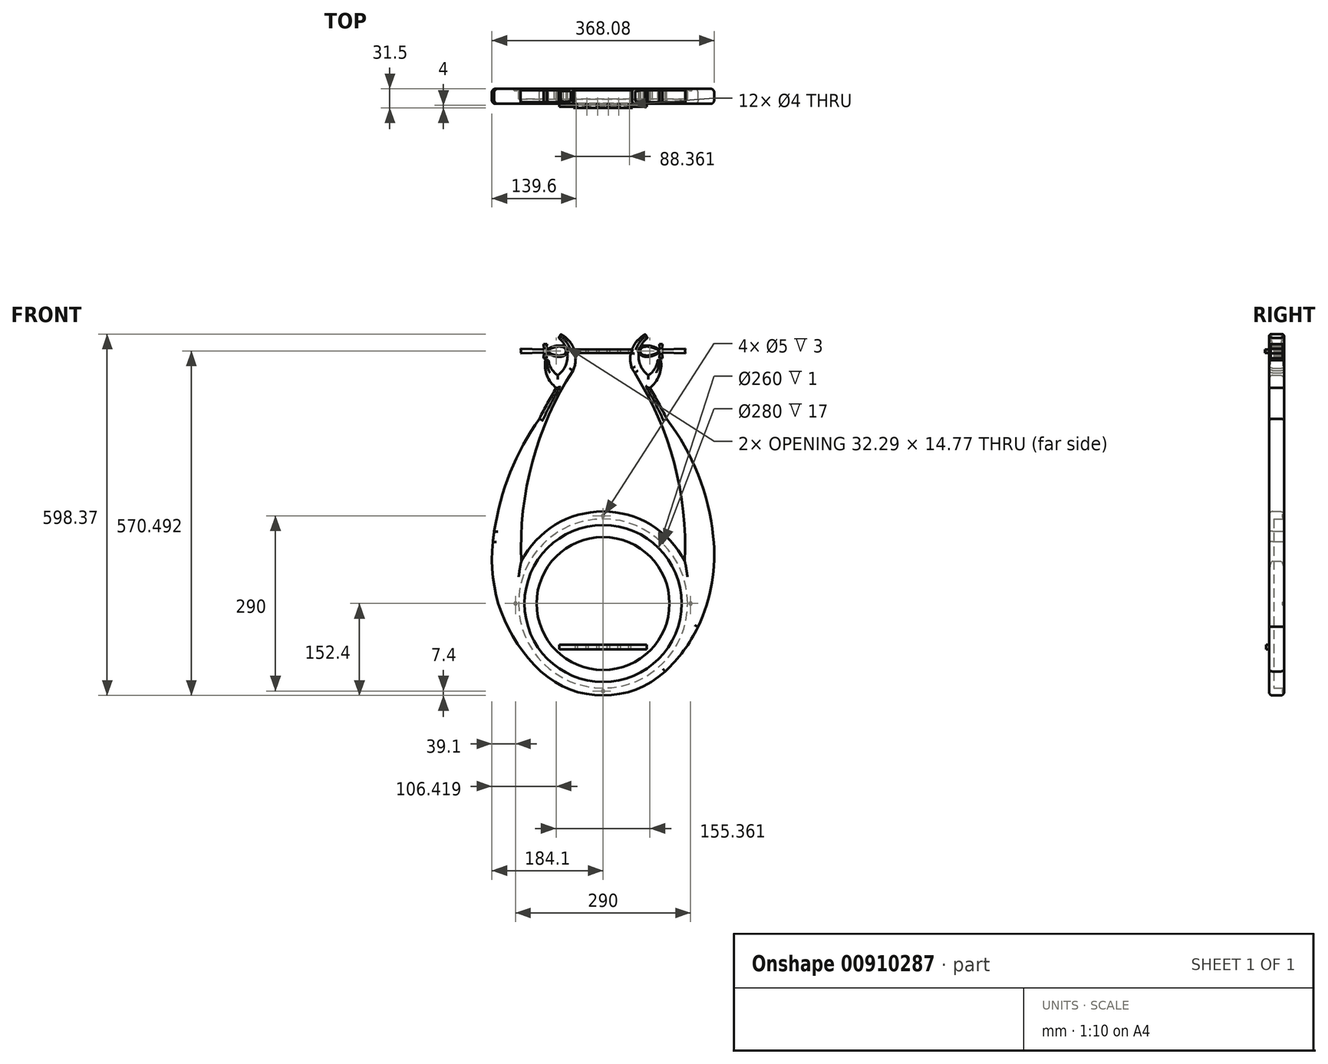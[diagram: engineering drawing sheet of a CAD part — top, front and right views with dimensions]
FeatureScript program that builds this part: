
annotation { "Feature Type Name" : "Feature", "Feature Type Description" : "" }
export const myFeature = defineFeature(function(context is Context, id is Id, definition is map)
    precondition{}
    {
        {
            var Q0;
            Q0=qCreatedBy(makeId("Front.planeOp"),FACE);
            var sketch = newSketch(context, id + "F0", { "sketchPlane" : qUnion([Q0])});
            skArc(sketch, "E0", {"start": v(-102.81, -112.5) * mm, "mid": v(0, -152.4) * mm, "end": v(102.81, -112.5) * mm});
            skArc(sketch, "E1", {"start": v(-77.27, 356.97) * mm, "mid": v(-91.95, 331.84) * mm, "end": v(-105.27, 305.96) * mm});
            skArc(sketch, "E2", {"start": v(105.27, 305.96) * mm, "mid": v(91.95, 331.84) * mm, "end": v(77.27, 356.97) * mm});
            skArc(sketch, "E3", {"start": v(-67.27, 356.97) * mm, "mid": v(-121.3, 218.22) * mm, "end": v(-135.37, 70) * mm});
            skLineSegment(sketch, "E4", {"start": v(0, 0) * mm, "end": v(0, 365.5) * mm, "construction": true});
            skArc(sketch, "E5", {"start": v(-49.84, 385.97) * mm, "mid": v(-58.78, 371.6) * mm, "end": v(-67.27, 356.97) * mm});
            skArc(sketch, "E6", {"start": v(-53.11, 430.97) * mm, "mid": v(-60.83, 439.18) * mm, "end": v(-69.82, 445.97) * mm});
            skLineSegment(sketch, "E7", {"start": v(-69.82, 445.97) * mm, "end": v(-73.43, 439.97) * mm});
            skArc(sketch, "E8", {"start": v(-75.07, 377.97) * mm, "mid": v(-58.76, 408.56) * mm, "end": v(-73.43, 439.97) * mm});
            skPoint(sketch, "E9.orphan", {"position": v(-39.82, 400.97) * mm});
            skArc(sketch, "E10", {"start": v(-90.57, 402.97) * mm, "mid": v(-85.57, 388.76) * mm, "end": v(-75.07, 377.97) * mm});
            skLineSegment(sketch, "E11", {"start": v(-90.57, 402.97) * mm, "end": v(-95.57, 402.97) * mm});
            skArc(sketch, "E12", {"start": v(-95.57, 402.97) * mm, "mid": v(-92.8, 377.42) * mm, "end": v(-77.27, 356.97) * mm});
            skArc(sketch, "E13", {"start": v(-50.7, 426.92) * mm, "mid": v(-51.87, 428.97) * mm, "end": v(-53.11, 430.97) * mm});
            skArc(sketch, "E14.MirrorCS", {"start": v(67.27, 356.97) * mm, "mid": v(121.3, 218.22) * mm, "end": v(135.37, 70) * mm});
            skArc(sketch, "E15.MirrorCS", {"start": v(95.57, 402.97) * mm, "mid": v(92.8, 377.42) * mm, "end": v(77.27, 356.97) * mm});
            skArc(sketch, "E16.MirrorCS", {"start": v(90.57, 402.97) * mm, "mid": v(85.57, 388.76) * mm, "end": v(75.07, 377.97) * mm});
            skLineSegment(sketch, "E17.MirrorCS", {"start": v(90.57, 402.97) * mm, "end": v(95.57, 402.97) * mm});
            skArc(sketch, "E18.MirrorCS", {"start": v(75.07, 377.97) * mm, "mid": v(58.76, 408.56) * mm, "end": v(73.43, 439.97) * mm});
            skLineSegment(sketch, "E19.MirrorCS", {"start": v(69.82, 445.97) * mm, "end": v(73.43, 439.97) * mm});
            skArc(sketch, "E20.MirrorCS", {"start": v(53.11, 430.97) * mm, "mid": v(60.83, 439.18) * mm, "end": v(69.82, 445.97) * mm});
            skArc(sketch, "E21.MirrorCS", {"start": v(45.98, 415.18) * mm, "mid": v(48.94, 423.35) * mm, "end": v(53.11, 430.97) * mm});
            skArc(sketch, "E22.MirrorCS", {"start": v(52.4, 381.97) * mm, "mid": v(49.96, 385.78) * mm, "end": v(47.74, 389.72) * mm});
            skArc(sketch, "E23.MirrorCS", {"start": v(49.84, 385.97) * mm, "mid": v(58.78, 371.6) * mm, "end": v(67.27, 356.97) * mm});
            skArc(sketch, "E24.trimOffspring", {"start": v(135.37, 70) * mm, "mid": v(0, 152.4) * mm, "end": v(-135.37, 70) * mm});
            skPoint(sketch, "E25.orphan", {"position": v(-44.02, 397.97) * mm});
            skArc(sketch, "E26", {"start": v(-49.84, 385.97) * mm, "mid": v(-45.46, 406.54) * mm, "end": v(-50.7, 426.92) * mm});
            skArc(sketch, "E27", {"start": v(45.98, 415.18) * mm, "mid": v(45.14, 402.33) * mm, "end": v(47.74, 389.72) * mm});
            skPoint(sketch, "E28.orphan", {"position": v(44.02, 397.97) * mm});
            skPoint(sketch, "E29.orphan", {"position": v(-153.73, 164.99) * mm});
            skPoint(sketch, "E30.orphan", {"position": v(150.74, 163.69) * mm});
            skArc(sketch, "E31", {"start": v(-182.37, 102.33) * mm, "mid": v(-168.4, -14.65) * mm, "end": v(-102.81, -112.5) * mm});
            skArc(sketch, "E32", {"start": v(102.81, -112.5) * mm, "mid": v(133.42, -78.1) * mm, "end": v(157.25, -38.7) * mm});
            skPoint(sketch, "E33.orphan", {"position": v(146.2, -43.03) * mm});
            skPoint(sketch, "E34.end.orphan", {"position": v(-146.2, -43.03) * mm});
            skArc(sketch, "E35", {"start": v(157.25, -38.7) * mm, "mid": v(180.1, 34.24) * mm, "end": v(182.37, 110.63) * mm});
            skPoint(sketch, "E35.startSnap0", {"position": v(157.25, 188.12) * mm});
            skArc(sketch, "E36", {"start": v(-180.13, 119.66) * mm, "mid": v(-181.4, 111) * mm, "end": v(-182.37, 102.33) * mm});
            skPoint(sketch, "E37.orphan", {"position": v(-162.96, 173.92) * mm});
            skPoint(sketch, "E38.orphan", {"position": v(160.9, 173.92) * mm});
            skArc(sketch, "E39", {"start": v(-105.27, 305.96) * mm, "mid": v(-156.8, 209.06) * mm, "end": v(-182.37, 102.33) * mm});
            skArc(sketch, "E40", {"start": v(182.37, 110.63) * mm, "mid": v(157.46, 213.68) * mm, "end": v(105.27, 305.96) * mm});
            skPoint(sketch, "E41.orphan", {"position": v(162.49, 188.3) * mm});
            skPoint(sketch, "E42.orphan", {"position": v(-159.18, 188.3) * mm});
            skSolve(sketch);
        }
        {
            var Q0;
            Q0 = qSketchRegion(id + "F0", true);
            extrude(context, id + "F1", {"entities" : qUnion([Q0]), "depth" : 25 * mm, "offsetDistance" : 25 * mm});
        }
        {
            var Q0;
            Q0=makeQuery(id+"F96qqXRXt9k63Jo_1.opFillet","SPLIT",FACE,{"disambiguationData":[OD(2.0)],"derivedFrom":makeQuery(id+"F1.opExtrude","CAP_FACE",FACE,{"disambiguationData":[OSD([sQuery(id+"F0.wireOp",EDGE,"E0"),sQuery(id+"F0.wireOp",EDGE,"E1"),sQuery(id+"F0.wireOp",EDGE,"E2"),sQuery(id+"F0.wireOp",EDGE,"E3"),sQuery(id+"F0.wireOp",EDGE,"E5"),sQuery(id+"F0.wireOp",EDGE,"E6"),sQuery(id+"F0.wireOp",EDGE,"E7"),sQuery(id+"F0.wireOp",EDGE,"E8"),sQuery(id+"F0.wireOp",EDGE,"E10"),sQuery(id+"F0.wireOp",EDGE,"E11"),sQuery(id+"F0.wireOp",EDGE,"E12"),sQuery(id+"F0.wireOp",EDGE,"E13"),sQuery(id+"F0.wireOp",EDGE,"E14.MirrorCS"),sQuery(id+"F0.wireOp",EDGE,"E15.MirrorCS"),sQuery(id+"F0.wireOp",EDGE,"E16.MirrorCS"),sQuery(id+"F0.wireOp",EDGE,"E17.MirrorCS"),sQuery(id+"F0.wireOp",EDGE,"E18.MirrorCS"),sQuery(id+"F0.wireOp",EDGE,"E19.MirrorCS"),sQuery(id+"F0.wireOp",EDGE,"E20.MirrorCS"),sQuery(id+"F0.wireOp",EDGE,"E21.MirrorCS"),sQuery(id+"F0.wireOp",EDGE,"E22.MirrorCS"),sQuery(id+"F0.wireOp",EDGE,"E23.MirrorCS"),sQuery(id+"F0.wireOp",EDGE,"E24.trimOffspring"),sQuery(id+"F0.wireOp",EDGE,"E26"),sQuery(id+"F0.wireOp",EDGE,"E27")])],"isStart":false})});
            var sketch = newSketch(context, id + "F2", { "sketchPlane" : qUnion([Q0])});
            skCircle(sketch, "E43", {"center": v(0, 0) * mm, "radius": 130 * mm});
            skCircle(sketch, "E44", {"center": v(0, 0) * mm, "radius": 110 * mm});
            skSolve(sketch);
        }
        {
            var Q0;
            Q0 = qSketchRegion(id + "F2", true);
            extrude(context, id + "F3", {"entities" : qUnion([Q0]), "operationType" : NewBodyOperationType.REMOVE, "oppositeDirection" : true, "depth" : 1 * mm, "offsetDistance" : 25 * mm});
        }
        {
            var Q0;
            Q0=makeQuery(id+"F96qqXRXt9k63Jo_1.opFillet","SPLIT",FACE,{"disambiguationData":[OD(2.0)],"derivedFrom":makeQuery(id+"F1.opExtrude","CAP_FACE",FACE,{"disambiguationData":[OSD([sQuery(id+"F0.wireOp",EDGE,"E0"),sQuery(id+"F0.wireOp",EDGE,"E1"),sQuery(id+"F0.wireOp",EDGE,"E2"),sQuery(id+"F0.wireOp",EDGE,"E3"),sQuery(id+"F0.wireOp",EDGE,"E5"),sQuery(id+"F0.wireOp",EDGE,"E6"),sQuery(id+"F0.wireOp",EDGE,"E7"),sQuery(id+"F0.wireOp",EDGE,"E8"),sQuery(id+"F0.wireOp",EDGE,"E10"),sQuery(id+"F0.wireOp",EDGE,"E11"),sQuery(id+"F0.wireOp",EDGE,"E12"),sQuery(id+"F0.wireOp",EDGE,"E13"),sQuery(id+"F0.wireOp",EDGE,"E14.MirrorCS"),sQuery(id+"F0.wireOp",EDGE,"E15.MirrorCS"),sQuery(id+"F0.wireOp",EDGE,"E16.MirrorCS"),sQuery(id+"F0.wireOp",EDGE,"E17.MirrorCS"),sQuery(id+"F0.wireOp",EDGE,"E18.MirrorCS"),sQuery(id+"F0.wireOp",EDGE,"E19.MirrorCS"),sQuery(id+"F0.wireOp",EDGE,"E20.MirrorCS"),sQuery(id+"F0.wireOp",EDGE,"E21.MirrorCS"),sQuery(id+"F0.wireOp",EDGE,"E22.MirrorCS"),sQuery(id+"F0.wireOp",EDGE,"E23.MirrorCS"),sQuery(id+"F0.wireOp",EDGE,"E24.trimOffspring"),sQuery(id+"F0.wireOp",EDGE,"E26"),sQuery(id+"F0.wireOp",EDGE,"E27")])],"isStart":true})});
            cPlane(context, id + "F4", {"entities" : qUnion([Q0]), "cplaneType" : CPlaneType.OFFSET, "offset" : 12.5 * mm, "oppositeDirection" : true, "width" : 150 * mm, "height" : 150 * mm});
        }
        {
            var Q0;
            Q0=qCreatedBy(id+"F4.planeOp",FACE);
            var sketch = newSketch(context, id + "F5", { "sketchPlane" : qUnion([Q0])});
            skLineSegment(sketch, "E45.bottom", {"start": v(-60.13, 415.18) * mm, "end": v(60.13, 415.18) * mm});
            skLineSegment(sketch, "E45.top", {"start": v(-60.13, 420.82) * mm, "end": v(60.13, 420.82) * mm});
            skPoint(sketch, "E45.middle", {"position": v(0, 418) * mm});
            skArc(sketch, "E46", {"start": v(62.57, 425.82) * mm, "mid": v(61.07, 423.46) * mm, "end": v(60.13, 420.82) * mm});
            skArc(sketch, "E47", {"start": v(93.83, 420.5) * mm, "mid": v(87.75, 423.53) * mm, "end": v(81.35, 425.82) * mm});
            skArc(sketch, "E48", {"start": v(81.35, 409.82) * mm, "mid": v(87.76, 412.29) * mm, "end": v(93.83, 415.5) * mm});
            skLineSegment(sketch, "E49", {"start": v(93.83, 420.5) * mm, "end": v(93, 429.81) * mm});
            skLineSegment(sketch, "E50", {"start": v(98.28, 429.84) * mm, "end": v(97.83, 420.5) * mm});
            skLineSegment(sketch, "E51", {"start": v(93.83, 415.5) * mm, "end": v(93.27, 406.17) * mm});
            skLineSegment(sketch, "E52", {"start": v(98.28, 406.16) * mm, "end": v(97.83, 415.5) * mm});
            skLineSegment(sketch, "E53", {"start": v(97.83, 415.5) * mm, "end": v(136.4, 414) * mm});
            skLineSegment(sketch, "E54", {"start": v(136.4, 422) * mm, "end": v(97.83, 420.5) * mm});
            skArc(sketch, "E55", {"start": v(136.4, 422) * mm, "mid": v(135.93, 418) * mm, "end": v(136.4, 414) * mm});
            skArc(sketch, "E56", {"start": v(93, 429.81) * mm, "mid": v(95.64, 429.62) * mm, "end": v(98.28, 429.84) * mm});
            skArc(sketch, "E57", {"start": v(98.28, 406.16) * mm, "mid": v(95.77, 406.35) * mm, "end": v(93.27, 406.17) * mm});
            skArc(sketch, "E58.trimOffspring", {"start": v(60.13, 415.18) * mm, "mid": v(61.07, 412.54) * mm, "end": v(62.57, 410.18) * mm});
            skLineSegment(sketch, "E59", {"start": v(0, 418) * mm, "end": v(0, 365.49) * mm, "construction": true});
            skArc(sketch, "E60.MirrorCS", {"start": v(-98.28, 406.16) * mm, "mid": v(-95.77, 406.35) * mm, "end": v(-93.27, 406.17) * mm});
            skArc(sketch, "E61.MirrorCS", {"start": v(-136.4, 422) * mm, "mid": v(-135.93, 418) * mm, "end": v(-136.4, 414) * mm});
            skArc(sketch, "E62.MirrorCS", {"start": v(-93, 429.81) * mm, "mid": v(-95.64, 429.62) * mm, "end": v(-98.28, 429.84) * mm});
            skLineSegment(sketch, "E63.MirrorCS", {"start": v(-98.28, 429.84) * mm, "end": v(-97.83, 420.5) * mm});
            skLineSegment(sketch, "E64.MirrorCS", {"start": v(-93.83, 415.5) * mm, "end": v(-93.27, 406.17) * mm});
            skArc(sketch, "E65.MirrorCS", {"start": v(-81.35, 409.82) * mm, "mid": v(-87.76, 412.29) * mm, "end": v(-93.83, 415.5) * mm});
            skLineSegment(sketch, "E66.MirrorCS", {"start": v(-93.83, 420.5) * mm, "end": v(-93, 429.81) * mm});
            skLineSegment(sketch, "E67.MirrorCS", {"start": v(-136.4, 422) * mm, "end": v(-97.83, 420.5) * mm});
            skLineSegment(sketch, "E68.MirrorCS", {"start": v(-97.83, 415.5) * mm, "end": v(-136.4, 414) * mm});
            skArc(sketch, "E69.MirrorCS", {"start": v(-93.83, 420.5) * mm, "mid": v(-87.75, 423.53) * mm, "end": v(-81.35, 425.82) * mm});
            skLineSegment(sketch, "E70.MirrorCS", {"start": v(-98.28, 406.16) * mm, "end": v(-97.83, 415.5) * mm});
            skArc(sketch, "E71.MirrorCS", {"start": v(-62.57, 425.82) * mm, "mid": v(-61.07, 423.46) * mm, "end": v(-60.13, 420.82) * mm});
            skArc(sketch, "E72.MirrorCS", {"start": v(-60.13, 415.18) * mm, "mid": v(-61.07, 412.54) * mm, "end": v(-62.57, 410.18) * mm});
            skArc(sketch, "E73", {"start": v(81.35, 425.82) * mm, "mid": v(71.96, 427.2) * mm, "end": v(62.57, 425.82) * mm});
            skPoint(sketch, "E73.startSnap0", {"position": v(62.57, 425.82) * mm});
            skArc(sketch, "E74", {"start": v(62.57, 410.18) * mm, "mid": v(71.93, 408.61) * mm, "end": v(81.35, 409.82) * mm});
            skPoint(sketch, "E74.startSnap0", {"position": v(82.44, 410.18) * mm});
            skPoint(sketch, "E75.orphan", {"position": v(64.98, 428.1) * mm});
            skPoint(sketch, "E76.orphan", {"position": v(66.07, 407.2) * mm});
            skArc(sketch, "E77.MirrorCS", {"start": v(-81.35, 425.82) * mm, "mid": v(-71.96, 427.2) * mm, "end": v(-62.57, 425.82) * mm});
            skArc(sketch, "E78.MirrorCS", {"start": v(-62.57, 410.18) * mm, "mid": v(-71.93, 408.61) * mm, "end": v(-81.35, 409.82) * mm});
            skPoint(sketch, "E79.orphan", {"position": v(-66.07, 407.2) * mm});
            skPoint(sketch, "E80.orphan", {"position": v(-64.98, 428.1) * mm});
            skPoint(sketch, "E81.orphan", {"position": v(85.85, 411.46) * mm});
            skPoint(sketch, "E82.orphan", {"position": v(-81.35, 425.82) * mm});
            skPoint(sketch, "E83.orphan", {"position": v(-85.85, 411.46) * mm});
            skSolve(sketch);
        }
        {
            var Q0;
            Q0 = qSketchRegion(id + "F5", true);
            extrude(context, id + "F6", {"entities" : qUnion([Q0]), "operationType" : NewBodyOperationType.ADD, "depth" : 10 * mm, "offsetDistance" : 25 * mm, "hasSecondDirection" : true, "secondDirectionOppositeDirection" : true, "secondDirectionDepth" : 10 * mm});
        }
        {
            var Q0;
            Q0=makeQuery(id+"F6.opExtrude","SWEPT_EDGE",EDGE,{"disambiguationData":[OSD([sQuery(id+"F5.wireOp",EDGE,"E58.trimOffspring"),sQuery(id+"F5.wireOp",EDGE,"E74")])]});
            var Q1;
            Q1=makeQuery(id+"F6.opExtrude","SWEPT_EDGE",EDGE,{"disambiguationData":[OSD([sQuery(id+"F5.wireOp",EDGE,"E46"),sQuery(id+"F5.wireOp",EDGE,"E73")])]});
            var Q2;
            Q2=makeQuery(id+"F6.opExtrude","SWEPT_EDGE",EDGE,{"disambiguationData":[OSD([sQuery(id+"F5.wireOp",EDGE,"E72.MirrorCS"),sQuery(id+"F5.wireOp",EDGE,"E78.MirrorCS")])]});
            var Q3;
            Q3=makeQuery(id+"F6.opExtrude","SWEPT_EDGE",EDGE,{"disambiguationData":[OSD([sQuery(id+"F5.wireOp",EDGE,"E71.MirrorCS"),sQuery(id+"F5.wireOp",EDGE,"E77.MirrorCS")])]});
            fillet(context, id + "F7", {"entities" : qUnion([Q0, Q1, Q2, Q3]), "radius" : 10 * mm, "tangentPropagation" : true, "allowEdgeOverflow" : false});
        }
        {
            var Q0;
            {var subQ0=sQuery(id+"F5.wireOp",EDGE,"E52");var subQ1=sQuery(id+"F5.wireOp",EDGE,"E51");var subQ2=sQuery(id+"F5.wireOp",EDGE,"E50");var subQ3=sQuery(id+"F5.wireOp",EDGE,"E74");var subQ4=sQuery(id+"F5.wireOp",EDGE,"E49");var subQ5=sQuery(id+"F5.wireOp",EDGE,"E73");var subQ6=sQuery(id+"F5.wireOp",EDGE,"E48");var subQ7=sQuery(id+"F5.wireOp",EDGE,"E47");var subQ9=sQuery(id+"F5.wireOp",EDGE,"E58.trimOffspring");var subQ10=sQuery(id+"F5.wireOp",EDGE,"E45.bottom");var subQ11=sQuery(id+"F5.wireOp",EDGE,"E45.top");var subQ12=sQuery(id+"F5.wireOp",EDGE,"E46");var subQ13=sQuery(id+"F5.wireOp",EDGE,"E53");var subQ14=sQuery(id+"F5.wireOp",EDGE,"E54");var subQ15=sQuery(id+"F5.wireOp",EDGE,"E55");var subQ16=sQuery(id+"F5.wireOp",EDGE,"E56");var subQ17=sQuery(id+"F5.wireOp",EDGE,"E57");Q0=makeQuery(id+"F6.boolean.opBoolean","SPLIT",FACE,{"disambiguationData":[TD([makeQuery(id+"F6.opExtrude","SWEPT_FACE",FACE,{"disambiguationData":[OSD([subQ12])]})])],"derivedFrom":makeQuery(id+"F6.opExtrude","CAP_FACE",FACE,{"disambiguationData":[OSD([subQ10,subQ11,subQ12,subQ7,subQ6,subQ4,subQ2,subQ1,subQ0,subQ13,subQ14,subQ15,subQ16,subQ17,subQ9,sQuery(id+"F5.wireOp",EDGE,"E60.MirrorCS"),sQuery(id+"F5.wireOp",EDGE,"E61.MirrorCS"),sQuery(id+"F5.wireOp",EDGE,"E62.MirrorCS"),sQuery(id+"F5.wireOp",EDGE,"E63.MirrorCS"),sQuery(id+"F5.wireOp",EDGE,"E64.MirrorCS"),sQuery(id+"F5.wireOp",EDGE,"E65.MirrorCS"),sQuery(id+"F5.wireOp",EDGE,"E66.MirrorCS"),sQuery(id+"F5.wireOp",EDGE,"E67.MirrorCS"),sQuery(id+"F5.wireOp",EDGE,"E68.MirrorCS"),sQuery(id+"F5.wireOp",EDGE,"E69.MirrorCS"),sQuery(id+"F5.wireOp",EDGE,"E70.MirrorCS"),sQuery(id+"F5.wireOp",EDGE,"E71.MirrorCS"),sQuery(id+"F5.wireOp",EDGE,"E72.MirrorCS"),subQ5,subQ3,sQuery(id+"F5.wireOp",EDGE,"E77.MirrorCS"),sQuery(id+"F5.wireOp",EDGE,"E78.MirrorCS")])],"isStart":true})});}
            var sketch = newSketch(context, id + "F8", { "sketchPlane" : qUnion([Q0])});
            skPoint(sketch, "E84", {"position": v(-93.83, 418.38) * mm});
            skPoint(sketch, "E84.positionSnap0", {"position": v(-58.06, 418.38) * mm});
            skArc(sketch, "E85", {"start": v(-77.83, 424.7) * mm, "mid": v(-86.09, 422.2) * mm, "end": v(-93.83, 418.38) * mm});
            skArc(sketch, "E86", {"start": v(-93.83, 418.38) * mm, "mid": v(-86.32, 413.66) * mm, "end": v(-77.83, 411.08) * mm});
            skArc(sketch, "E87", {"start": v(-66.05, 424.4) * mm, "mid": v(-71.92, 425.48) * mm, "end": v(-77.83, 424.7) * mm});
            skArc(sketch, "E88", {"start": v(-77.83, 411.08) * mm, "mid": v(-71.9, 410.74) * mm, "end": v(-66.05, 411.69) * mm});
            skArc(sketch, "E89", {"start": v(-66.05, 411.69) * mm, "mid": v(-61.54, 418.05) * mm, "end": v(-66.05, 424.4) * mm});
            skLineSegment(sketch, "E90", {"start": v(0, 410.89) * mm, "end": v(0, 363.53) * mm, "construction": true});
            skArc(sketch, "E91.MirrorCS", {"start": v(66.05, 411.69) * mm, "mid": v(61.54, 418.05) * mm, "end": v(66.05, 424.4) * mm});
            skArc(sketch, "E92.MirrorCS", {"start": v(93.83, 418.38) * mm, "mid": v(86.32, 413.66) * mm, "end": v(77.83, 411.08) * mm});
            skArc(sketch, "E93.MirrorCS", {"start": v(77.83, 424.7) * mm, "mid": v(86.09, 422.2) * mm, "end": v(93.83, 418.38) * mm});
            skArc(sketch, "E94.MirrorCS", {"start": v(66.05, 424.4) * mm, "mid": v(71.92, 425.48) * mm, "end": v(77.83, 424.7) * mm});
            skArc(sketch, "E95.MirrorCS", {"start": v(77.83, 411.08) * mm, "mid": v(71.9, 410.74) * mm, "end": v(66.05, 411.69) * mm});
            skPoint(sketch, "E96.MirrorP", {"position": v(58.06, 418.38) * mm});
            skPoint(sketch, "E97.MirrorP", {"position": v(93.83, 418.38) * mm});
            skSolve(sketch);
        }
        {
            var Q0;
            Q0 = qSketchRegion(id + "F8", true);
            extrude(context, id + "F9", {"entities" : qUnion([Q0]), "operationType" : NewBodyOperationType.REMOVE, "endBound" : BoundingType.THROUGH_ALL, "oppositeDirection" : true, "depth" : 25 * mm, "offsetDistance" : 25 * mm});
        }
        {
            var Q0;
            Q0=makeQuery(id+"F1.opExtrude","CAP_EDGE",EDGE,{"disambiguationData":[OSD([sQuery(id+"F0.wireOp",EDGE,"E18.MirrorCS")])],"isStart":false});
            var Q1;
            Q1=makeQuery(id+"F1.opExtrude","CAP_EDGE",EDGE,{"disambiguationData":[OSD([sQuery(id+"F0.wireOp",EDGE,"E32")])],"isStart":false});
            var Q2;
            Q2=makeQuery(id+"F1.opExtrude","CAP_EDGE",EDGE,{"disambiguationData":[OSD([sQuery(id+"F0.wireOp",EDGE,"E2")])],"isStart":false});
            var Q3;
            Q3=makeQuery(id+"F1.opExtrude","CAP_EDGE",EDGE,{"disambiguationData":[OSD([sQuery(id+"F0.wireOp",EDGE,"E40")])],"isStart":false});
            var Q4;
            Q4=makeQuery(id+"F1.opExtrude","CAP_EDGE",EDGE,{"disambiguationData":[OSD([sQuery(id+"F0.wireOp",EDGE,"E35")])],"isStart":false});
            var Q5;
            Q5=makeQuery(id+"F1.opExtrude","CAP_EDGE",EDGE,{"disambiguationData":[OSD([sQuery(id+"F0.wireOp",EDGE,"E15.MirrorCS")])],"isStart":false});
            var Q6;
            Q6=makeQuery(id+"F1.opExtrude","CAP_EDGE",EDGE,{"disambiguationData":[OSD([sQuery(id+"F0.wireOp",EDGE,"E0")])],"isStart":false});
            var Q7;
            Q7=makeQuery(id+"F1.opExtrude","CAP_EDGE",EDGE,{"disambiguationData":[OSD([sQuery(id+"F0.wireOp",EDGE,"E27")])],"isStart":false});
            var Q8;
            Q8=makeQuery(id+"F1.opExtrude","CAP_EDGE",EDGE,{"disambiguationData":[OSD([sQuery(id+"F0.wireOp",EDGE,"E14.MirrorCS"),sQuery(id+"F0.wireOp",EDGE,"E23.MirrorCS")])],"isStart":false});
            var Q9;
            Q9=makeQuery(id+"F1.opExtrude","CAP_EDGE",EDGE,{"disambiguationData":[OSD([sQuery(id+"F0.wireOp",EDGE,"E16.MirrorCS")])],"isStart":false});
            var Q10;
            Q10=makeQuery(id+"F1.opExtrude","CAP_EDGE",EDGE,{"disambiguationData":[OSD([sQuery(id+"F0.wireOp",EDGE,"E20.MirrorCS")])],"isStart":false});
            var Q11;
            Q11=makeQuery(id+"F1.opExtrude","CAP_EDGE",EDGE,{"disambiguationData":[OSD([sQuery(id+"F0.wireOp",EDGE,"E19.MirrorCS")])],"isStart":false});
            var Q12;
            Q12=makeQuery(id+"F1.opExtrude","CAP_EDGE",EDGE,{"disambiguationData":[OSD([sQuery(id+"F0.wireOp",EDGE,"E21.MirrorCS")])],"isStart":false});
            var Q13;
            Q13=makeQuery(id+"F1.opExtrude","CAP_EDGE",EDGE,{"disambiguationData":[OSD([sQuery(id+"F0.wireOp",EDGE,"E17.MirrorCS")])],"isStart":false});
            var Q14;
            Q14=makeQuery(id+"F1.opExtrude","CAP_EDGE",EDGE,{"disambiguationData":[OSD([sQuery(id+"F0.wireOp",EDGE,"E24.trimOffspring")])],"isStart":false});
            var Q15;
            Q15=makeQuery(id+"F1.opExtrude","CAP_EDGE",EDGE,{"disambiguationData":[OSD([sQuery(id+"F0.wireOp",EDGE,"E26")])],"isStart":false});
            var Q16;
            Q16=makeQuery(id+"F1.opExtrude","CAP_EDGE",EDGE,{"disambiguationData":[OSD([sQuery(id+"F0.wireOp",EDGE,"E6")])],"isStart":false});
            var Q17;
            Q17=makeQuery(id+"F1.opExtrude","CAP_EDGE",EDGE,{"disambiguationData":[OSD([sQuery(id+"F0.wireOp",EDGE,"E3"),sQuery(id+"F0.wireOp",EDGE,"E5")])],"isStart":false});
            var Q18;
            Q18=makeQuery(id+"F1.opExtrude","CAP_EDGE",EDGE,{"disambiguationData":[OSD([sQuery(id+"F0.wireOp",EDGE,"E13")])],"isStart":false});
            var Q19;
            Q19=makeQuery(id+"F1.opExtrude","CAP_EDGE",EDGE,{"disambiguationData":[OSD([sQuery(id+"F0.wireOp",EDGE,"E22.MirrorCS")])],"isStart":false});
            var Q20;
            Q20=makeQuery(id+"F1.opExtrude","CAP_EDGE",EDGE,{"disambiguationData":[OSD([sQuery(id+"F0.wireOp",EDGE,"E39")])],"isStart":false});
            var Q21;
            Q21=makeQuery(id+"F1.opExtrude","CAP_EDGE",EDGE,{"disambiguationData":[OSD([sQuery(id+"F0.wireOp",EDGE,"E36")])],"isStart":false});
            var Q22;
            Q22=makeQuery(id+"F1.opExtrude","CAP_EDGE",EDGE,{"disambiguationData":[OSD([sQuery(id+"F0.wireOp",EDGE,"E12")])],"isStart":false});
            var Q23;
            Q23=makeQuery(id+"F1.opExtrude","CAP_EDGE",EDGE,{"disambiguationData":[OSD([sQuery(id+"F0.wireOp",EDGE,"E10")])],"isStart":false});
            var Q24;
            Q24=makeQuery(id+"F1.opExtrude","CAP_EDGE",EDGE,{"disambiguationData":[OSD([sQuery(id+"F0.wireOp",EDGE,"E31")])],"isStart":false});
            var Q25;
            Q25=makeQuery(id+"F1.opExtrude","CAP_EDGE",EDGE,{"disambiguationData":[OSD([sQuery(id+"F0.wireOp",EDGE,"E7")])],"isStart":false});
            var Q26;
            Q26=makeQuery(id+"F1.opExtrude","CAP_EDGE",EDGE,{"disambiguationData":[OSD([sQuery(id+"F0.wireOp",EDGE,"E1")])],"isStart":false});
            var Q27;
            Q27=makeQuery(id+"F1.opExtrude","CAP_EDGE",EDGE,{"disambiguationData":[OSD([sQuery(id+"F0.wireOp",EDGE,"E8")])],"isStart":false});
            var Q28;
            Q28=makeQuery(id+"F1.opExtrude","CAP_EDGE",EDGE,{"disambiguationData":[OSD([sQuery(id+"F0.wireOp",EDGE,"E11")])],"isStart":false});
            fillet(context, id + "F10", {"entities" : qUnion([Q0, Q1, Q2, Q3, Q4, Q5, Q6, Q7, Q8, Q9, Q10, Q11, Q12, Q13, Q14, Q15, Q16, Q17, Q18, Q19, Q20, Q21, Q22, Q23, Q24, Q25, Q26, Q27, Q28]), "radius" : 6 * mm, "tangentPropagation" : true, "allowEdgeOverflow" : false});
        }
        {
            var Q0;
            {var subQ0=sQuery(id+"F0.wireOp",EDGE,"E24.trimOffspring");var subQ1=sQuery(id+"F0.wireOp",EDGE,"E22.MirrorCS");var subQ2=sQuery(id+"F0.wireOp",EDGE,"E21.MirrorCS");var subQ3=sQuery(id+"F0.wireOp",EDGE,"E20.MirrorCS");var subQ4=sQuery(id+"F0.wireOp",EDGE,"E19.MirrorCS");var subQ5=sQuery(id+"F0.wireOp",EDGE,"E18.MirrorCS");var subQ6=sQuery(id+"F0.wireOp",EDGE,"E17.MirrorCS");var subQ7=sQuery(id+"F0.wireOp",EDGE,"E16.MirrorCS");var subQ8=sQuery(id+"F0.wireOp",EDGE,"E15.MirrorCS");var subQ9=sQuery(id+"F0.wireOp",EDGE,"E23.MirrorCS");var subQ10=sQuery(id+"F0.wireOp",EDGE,"E14.MirrorCS");var subQ11=sQuery(id+"F0.wireOp",EDGE,"E13");var subQ12=sQuery(id+"F0.wireOp",EDGE,"E2");var subQ13=sQuery(id+"F0.wireOp",EDGE,"E1");var subQ14=sQuery(id+"F0.wireOp",EDGE,"E5");var subQ15=sQuery(id+"F0.wireOp",EDGE,"E3");var subQ16=sQuery(id+"F0.wireOp",EDGE,"E26");var subQ17=sQuery(id+"F0.wireOp",EDGE,"E0");var subQ18=sQuery(id+"F0.wireOp",EDGE,"E12");var subQ19=sQuery(id+"F0.wireOp",EDGE,"E6");var subQ20=sQuery(id+"F0.wireOp",EDGE,"E7");var subQ21=sQuery(id+"F0.wireOp",EDGE,"E8");var subQ22=sQuery(id+"F0.wireOp",EDGE,"E10");var subQ23=sQuery(id+"F0.wireOp",EDGE,"E11");var subQ24=sQuery(id+"F0.wireOp",EDGE,"E27");var subQ25=sQuery(id+"F0.wireOp",EDGE,"E31");var subQ26=sQuery(id+"F0.wireOp",EDGE,"E32");var subQ27=sQuery(id+"F0.wireOp",EDGE,"E35");var subQ28=sQuery(id+"F0.wireOp",EDGE,"E36");var subQ29=sQuery(id+"F0.wireOp",EDGE,"E39");var subQ30=sQuery(id+"F0.wireOp",EDGE,"E40");Q0=makeQuery(id+"FXKQqumeNgOc6mp_1.1.F3.boolean.opBoolean","SPLIT",FACE,{"disambiguationData":[TD([makeQuery(id+"F1.opExtrude","SWEPT_FACE",FACE,{"disambiguationData":[OSD([subQ17])]})])],"derivedFrom":makeQuery(id+"F1.opExtrude","CAP_FACE",FACE,{"disambiguationData":[OSD([subQ17,subQ13,subQ12,subQ15,subQ14,subQ19,subQ20,subQ21,subQ22,subQ23,subQ18,subQ11,subQ10,subQ8,subQ7,subQ6,subQ5,subQ4,subQ3,subQ2,subQ1,subQ9,subQ0,subQ16,subQ24,subQ25,subQ26,subQ27,subQ28,subQ29,subQ30])],"isStart":true})});}
            fillet(context, id + "F11", {"entities" : qUnion([Q0]), "radius" : 6 * mm, "tangentPropagation" : true, "allowEdgeOverflow" : false});
        }
        {
            var Q0;
            Q0=makeQuery(id+"F3.boolean.opBoolean","SPLIT",FACE,{"disambiguationData":[TD([makeQuery(id+"F3.opExtrude","SWEPT_FACE",FACE,{"disambiguationData":[OSD([sQuery(id+"F2.wireOp",EDGE,"E44")])]})])],"derivedFrom":makeQuery(id+"F1.opExtrude","CAP_FACE",FACE,{"disambiguationData":[OSD([sQuery(id+"F0.wireOp",EDGE,"E0"),sQuery(id+"F0.wireOp",EDGE,"E1"),sQuery(id+"F0.wireOp",EDGE,"E2"),sQuery(id+"F0.wireOp",EDGE,"E3"),sQuery(id+"F0.wireOp",EDGE,"E5"),sQuery(id+"F0.wireOp",EDGE,"E6"),sQuery(id+"F0.wireOp",EDGE,"E7"),sQuery(id+"F0.wireOp",EDGE,"E8"),sQuery(id+"F0.wireOp",EDGE,"E10"),sQuery(id+"F0.wireOp",EDGE,"E11"),sQuery(id+"F0.wireOp",EDGE,"E12"),sQuery(id+"F0.wireOp",EDGE,"E13"),sQuery(id+"F0.wireOp",EDGE,"E14.MirrorCS"),sQuery(id+"F0.wireOp",EDGE,"E15.MirrorCS"),sQuery(id+"F0.wireOp",EDGE,"E16.MirrorCS"),sQuery(id+"F0.wireOp",EDGE,"E17.MirrorCS"),sQuery(id+"F0.wireOp",EDGE,"E18.MirrorCS"),sQuery(id+"F0.wireOp",EDGE,"E19.MirrorCS"),sQuery(id+"F0.wireOp",EDGE,"E20.MirrorCS"),sQuery(id+"F0.wireOp",EDGE,"E21.MirrorCS"),sQuery(id+"F0.wireOp",EDGE,"E22.MirrorCS"),sQuery(id+"F0.wireOp",EDGE,"E23.MirrorCS"),sQuery(id+"F0.wireOp",EDGE,"E24.trimOffspring"),sQuery(id+"F0.wireOp",EDGE,"E26"),sQuery(id+"F0.wireOp",EDGE,"E27"),sQuery(id+"F0.wireOp",EDGE,"E31"),sQuery(id+"F0.wireOp",EDGE,"E32"),sQuery(id+"F0.wireOp",EDGE,"E35"),sQuery(id+"F0.wireOp",EDGE,"E36"),sQuery(id+"F0.wireOp",EDGE,"E39"),sQuery(id+"F0.wireOp",EDGE,"E40")])],"isStart":false})});
            var sketch = newSketch(context, id + "F12", { "sketchPlane" : qUnion([Q0])});
            skLineSegment(sketch, "E98.bottom", {"start": v(72.5, -76.2) * mm, "end": v(-72.5, -76.2) * mm});
            skLineSegment(sketch, "E98.top", {"start": v(72.5, -68.2) * mm, "end": v(-72.5, -68.2) * mm});
            skLineSegment(sketch, "E98.left", {"start": v(72.5, -76.2) * mm, "end": v(72.5, -68.2) * mm});
            skLineSegment(sketch, "E98.right", {"start": v(-72.5, -76.2) * mm, "end": v(-72.5, -68.2) * mm});
            skPoint(sketch, "E98.middle", {"position": v(0, -72.2) * mm});
            skSolve(sketch);
        }
        {
            var Q0;
            Q0 = qSketchRegion(id + "F12", true);
            extrude(context, id + "F13", {"entities" : qUnion([Q0]), "operationType" : NewBodyOperationType.ADD, "depth" : 5 * mm, "offsetDistance" : 25 * mm});
        }
        {
            var Q0;
            {var subQ0=sQuery(id+"F5.wireOp",EDGE,"E45.bottom");var subQ1=sQuery(id+"F5.wireOp",EDGE,"E45.top");Q0=makeQuery(id+"F6.boolean.opBoolean","SPLIT",FACE,{"disambiguationData":[TD([makeQuery(id+"F1.opExtrude","SWEPT_FACE",FACE,{"disambiguationData":[OSD([sQuery(id+"F0.wireOp",EDGE,"E21.MirrorCS")])]})])],"derivedFrom":makeQuery(id+"F6.opExtrude","CAP_FACE",FACE,{"disambiguationData":[OSD([subQ0,subQ1,sQuery(id+"F5.wireOp",EDGE,"E46"),sQuery(id+"F5.wireOp",EDGE,"E47"),sQuery(id+"F5.wireOp",EDGE,"E48"),sQuery(id+"F5.wireOp",EDGE,"E49"),sQuery(id+"F5.wireOp",EDGE,"E50"),sQuery(id+"F5.wireOp",EDGE,"E51"),sQuery(id+"F5.wireOp",EDGE,"E52"),sQuery(id+"F5.wireOp",EDGE,"E53"),sQuery(id+"F5.wireOp",EDGE,"E54"),sQuery(id+"F5.wireOp",EDGE,"E55"),sQuery(id+"F5.wireOp",EDGE,"E56"),sQuery(id+"F5.wireOp",EDGE,"E57"),sQuery(id+"F5.wireOp",EDGE,"E58.trimOffspring"),sQuery(id+"F5.wireOp",EDGE,"E60.MirrorCS"),sQuery(id+"F5.wireOp",EDGE,"E61.MirrorCS"),sQuery(id+"F5.wireOp",EDGE,"E62.MirrorCS"),sQuery(id+"F5.wireOp",EDGE,"E63.MirrorCS"),sQuery(id+"F5.wireOp",EDGE,"E64.MirrorCS"),sQuery(id+"F5.wireOp",EDGE,"E65.MirrorCS"),sQuery(id+"F5.wireOp",EDGE,"E66.MirrorCS"),sQuery(id+"F5.wireOp",EDGE,"E67.MirrorCS"),sQuery(id+"F5.wireOp",EDGE,"E68.MirrorCS"),sQuery(id+"F5.wireOp",EDGE,"E69.MirrorCS"),sQuery(id+"F5.wireOp",EDGE,"E70.MirrorCS"),sQuery(id+"F5.wireOp",EDGE,"E71.MirrorCS"),sQuery(id+"F5.wireOp",EDGE,"E72.MirrorCS"),sQuery(id+"F5.wireOp",EDGE,"E73"),sQuery(id+"F5.wireOp",EDGE,"E74"),sQuery(id+"F5.wireOp",EDGE,"E77.MirrorCS"),sQuery(id+"F5.wireOp",EDGE,"E78.MirrorCS")])],"isStart":true})});}
            extrude(context, id + "F14", {"entities" : qUnion([Q0]), "operationType" : NewBodyOperationType.ADD, "depth" : 9 * mm, "offsetDistance" : 25 * mm});
        }
        {
            var Q0;
            Q0=makeQuery(id+"F11.opFillet","SPLIT",FACE,{"disambiguationData":[OD(2.0)],"derivedFrom":makeQuery(id+"F1.opExtrude","CAP_FACE",FACE,{"disambiguationData":[OSD([sQuery(id+"F0.wireOp",EDGE,"E0"),sQuery(id+"F0.wireOp",EDGE,"E1"),sQuery(id+"F0.wireOp",EDGE,"E2"),sQuery(id+"F0.wireOp",EDGE,"E3"),sQuery(id+"F0.wireOp",EDGE,"E5"),sQuery(id+"F0.wireOp",EDGE,"E6"),sQuery(id+"F0.wireOp",EDGE,"E7"),sQuery(id+"F0.wireOp",EDGE,"E8"),sQuery(id+"F0.wireOp",EDGE,"E10"),sQuery(id+"F0.wireOp",EDGE,"E11"),sQuery(id+"F0.wireOp",EDGE,"E12"),sQuery(id+"F0.wireOp",EDGE,"E13"),sQuery(id+"F0.wireOp",EDGE,"E14.MirrorCS"),sQuery(id+"F0.wireOp",EDGE,"E15.MirrorCS"),sQuery(id+"F0.wireOp",EDGE,"E16.MirrorCS"),sQuery(id+"F0.wireOp",EDGE,"E17.MirrorCS"),sQuery(id+"F0.wireOp",EDGE,"E18.MirrorCS"),sQuery(id+"F0.wireOp",EDGE,"E19.MirrorCS"),sQuery(id+"F0.wireOp",EDGE,"E20.MirrorCS"),sQuery(id+"F0.wireOp",EDGE,"E21.MirrorCS"),sQuery(id+"F0.wireOp",EDGE,"E22.MirrorCS"),sQuery(id+"F0.wireOp",EDGE,"E23.MirrorCS"),sQuery(id+"F0.wireOp",EDGE,"E24.trimOffspring"),sQuery(id+"F0.wireOp",EDGE,"E26"),sQuery(id+"F0.wireOp",EDGE,"E27"),sQuery(id+"F0.wireOp",EDGE,"E31"),sQuery(id+"F0.wireOp",EDGE,"E32"),sQuery(id+"F0.wireOp",EDGE,"E35"),sQuery(id+"F0.wireOp",EDGE,"E36"),sQuery(id+"F0.wireOp",EDGE,"E39"),sQuery(id+"F0.wireOp",EDGE,"E40")])],"isStart":true})});
            var sketch = newSketch(context, id + "F15", { "sketchPlane" : qUnion([Q0])});
            skCircle(sketch, "E99", {"center": v(0, 0) * mm, "radius": 140 * mm});
            skSolve(sketch);
        }
        {
            var Q0;
            Q0 = qSketchRegion(id + "F15", true);
            extrude(context, id + "F16", {"entities" : qUnion([Q0]), "operationType" : NewBodyOperationType.REMOVE, "oppositeDirection" : true, "depth" : 17 * mm, "offsetDistance" : 25 * mm});
        }
        {
            var Q0;
            Q0=makeQuery(id+"F13.opExtrude","SWEPT_FACE",FACE,{"disambiguationData":[OSD([sQuery(id+"F12.wireOp",EDGE,"E98.bottom")])]});
            var sketch = newSketch(context, id + "F17", { "sketchPlane" : qUnion([Q0])});
            skCircle(sketch, "E100", {"center": v(-44.5, 27.5) * mm, "radius": 2 * mm});
            skCircle(sketch, "E101.1.0.0", {"center": v(-26.83, 27.5) * mm, "radius": 2 * mm});
            skCircle(sketch, "E101.2.0.0", {"center": v(-9.16, 27.5) * mm, "radius": 2 * mm});
            skCircle(sketch, "E101.3.0.0", {"center": v(8.52, 27.5) * mm, "radius": 2 * mm});
            skCircle(sketch, "E101.4.0.0", {"center": v(26.19, 27.5) * mm, "radius": 2 * mm});
            skCircle(sketch, "E101.5.0.0", {"center": v(43.86, 27.5) * mm, "radius": 2 * mm});
            skLineSegment(sketch, "E101.direction1", {"start": v(-66.83, 27.5) * mm, "end": v(-41.83, 27.5) * mm, "construction": true});
            skSolve(sketch);
        }
        {
            var Q0;
            Q0 = qSketchRegion(id + "F17", true);
            extrude(context, id + "F18", {"entities" : qUnion([Q0]), "operationType" : NewBodyOperationType.REMOVE, "endBound" : BoundingType.THROUGH_ALL, "oppositeDirection" : true, "depth" : 498 * mm, "offsetDistance" : 25 * mm});
        }
        {
            var Q0;
            Q0=makeQuery(id+"F11.opFillet","SPLIT",FACE,{"disambiguationData":[OD(2.0)],"derivedFrom":makeQuery(id+"F1.opExtrude","CAP_FACE",FACE,{"disambiguationData":[OSD([sQuery(id+"F0.wireOp",EDGE,"E0"),sQuery(id+"F0.wireOp",EDGE,"E1"),sQuery(id+"F0.wireOp",EDGE,"E2"),sQuery(id+"F0.wireOp",EDGE,"E3"),sQuery(id+"F0.wireOp",EDGE,"E5"),sQuery(id+"F0.wireOp",EDGE,"E6"),sQuery(id+"F0.wireOp",EDGE,"E7"),sQuery(id+"F0.wireOp",EDGE,"E8"),sQuery(id+"F0.wireOp",EDGE,"E10"),sQuery(id+"F0.wireOp",EDGE,"E11"),sQuery(id+"F0.wireOp",EDGE,"E12"),sQuery(id+"F0.wireOp",EDGE,"E13"),sQuery(id+"F0.wireOp",EDGE,"E14.MirrorCS"),sQuery(id+"F0.wireOp",EDGE,"E15.MirrorCS"),sQuery(id+"F0.wireOp",EDGE,"E16.MirrorCS"),sQuery(id+"F0.wireOp",EDGE,"E17.MirrorCS"),sQuery(id+"F0.wireOp",EDGE,"E18.MirrorCS"),sQuery(id+"F0.wireOp",EDGE,"E19.MirrorCS"),sQuery(id+"F0.wireOp",EDGE,"E20.MirrorCS"),sQuery(id+"F0.wireOp",EDGE,"E21.MirrorCS"),sQuery(id+"F0.wireOp",EDGE,"E22.MirrorCS"),sQuery(id+"F0.wireOp",EDGE,"E23.MirrorCS"),sQuery(id+"F0.wireOp",EDGE,"E24.trimOffspring"),sQuery(id+"F0.wireOp",EDGE,"E26"),sQuery(id+"F0.wireOp",EDGE,"E27"),sQuery(id+"F0.wireOp",EDGE,"E31"),sQuery(id+"F0.wireOp",EDGE,"E32"),sQuery(id+"F0.wireOp",EDGE,"E35"),sQuery(id+"F0.wireOp",EDGE,"E36"),sQuery(id+"F0.wireOp",EDGE,"E39"),sQuery(id+"F0.wireOp",EDGE,"E40")])],"isStart":true})});
            var sketch = newSketch(context, id + "F19", { "sketchPlane" : qUnion([Q0])});
            skCircle(sketch, "E102", {"center": v(0, 145) * mm, "radius": 2.5 * mm});
            skCircle(sketch, "E103", {"center": v(0, -145) * mm, "radius": 2.5 * mm});
            skCircle(sketch, "E104", {"center": v(-145, 0) * mm, "radius": 2.5 * mm});
            skCircle(sketch, "E105", {"center": v(145, 0) * mm, "radius": 2.5 * mm});
            skSolve(sketch);
        }
        {
            var Q0;
            Q0 = qSketchRegion(id + "F19", true);
            extrude(context, id + "F20", {"entities" : qUnion([Q0]), "operationType" : NewBodyOperationType.REMOVE, "oppositeDirection" : true, "depth" : 3 * mm, "offsetDistance" : 25 * mm});
        }
    });
